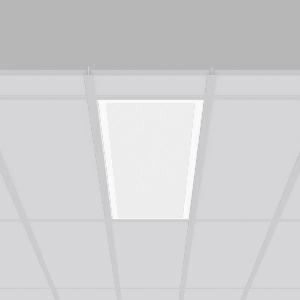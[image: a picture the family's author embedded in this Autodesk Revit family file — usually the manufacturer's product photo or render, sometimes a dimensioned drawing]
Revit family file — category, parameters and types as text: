
# Revit family: sidelite_eco_672375_002_04_02e4
name_source: partatom
category: Lighting Fixtures
units: mm (PartAtom-declared; Revit-internal decimal feet)

## family parameters
Cut with Voids When Loaded = No
Host = Face
Light Source = No
Part Type = Normal
Room Calculation Point = No
Round Connector Dimension = Use Diameter
Shared = No

## types (1)
- SIDELITE ECO (1 x LED Modul 830, 3150 lm, 3000)
    Apparent Load = 29 VA
    CIE Flux Codes = 60 87 97 100 100
    Color Rendering = 80
    Color Temperature = 3000
    Default Elevation = 1800 mm
    Description = Series: SIDELITE ECO
Highly economical recessed luminaire with progressive LED technology. For escape route illumination. Frame made of aluminium, powder-coated. Diffuser plastic microprismatic. Lightguide and diffuser made of non-yellowing plastic (PMMA). Lateral light emission (RZB SIDELITE technology) for homogeneous light distribution. External driver. Self-contained system with automatic self-test and feedback to the RZB monitoring system MULTIDIGIT. External driver with simple plug-in locking system. Extended connection cable (1.90 m). 
Colour: white
Length: 1245 mm
Width: 308 mm
Cut-out length: 1220 mm
Cut-out width: 285 mm
Recess height: 160 mm
Luminaire: recess height: 40 mm
Weight: 4.7 kg
Operating mode: maintained power mode
Duration time: 8 h
Lamp: LED
Socket: without socket
Colour temperature: 3000K
Colour rendering index (CRI): 80
System power: 29 W
Rated luminous flux: 3150 lm
Luminous flux, emergency: 210 lm
System power, emergency: -
Control gear: Regulated power supply
Protection class: I
Type of protection: IP 40
    Height = 0 mm  [stored 0 ft]
    Lamp = 1 x LED Modul 830
    Lamp Light Flux = 3150 lm
    Lamp count = 1
    Length = 1245 mm
    Lifetime = 50000 h
    Luminous efficacy = 109 lm/W
    Manufacturer = RZB
    ModVariant = No
    Model = 672375.002.04
    Mounting Place = Ceiling
    Mounting Type = Recessed
    Number of Poles = 1
    OnlyDefault = Yes
    Power Factor = 1
    Product Name = SIDELITE ECO
    Product group = Recessed modular luminaires
    ProductGroupID = 406
    Protection Class = Protection class I
    Protection Degree = IP 40
    RLX_Detail_Level = 1
    RLX_Emergency_Light_Flux = 210 lm
    RLX_Emergency_Type = 3
    RLX_Emergency_Type_DB = Yes
    RlxData = <blob elided: 34149 chars, md5=1d647af0>
    Socket = socket
    Standby Power = 0 W
    System Light Flux = 3150 lm
    System Power = 29 W
    Type Comments = Product without accessories
    Type Image = 312368.002.jpg
    URL = http://relux.com
    VarID = ---
    Voltage = 230 V
    Voltage Range = 220-240 V
    Weight = 0.00 kg
    Width = 308 mm

note: [stored X ft] marks values corroborated as IEEE doubles in the binary element streams (Revit-internal decimal feet)

## geometry (parser evidence)
native form markers: Blend x4, Sweep x12
no freeform markers — native parametric forms only
